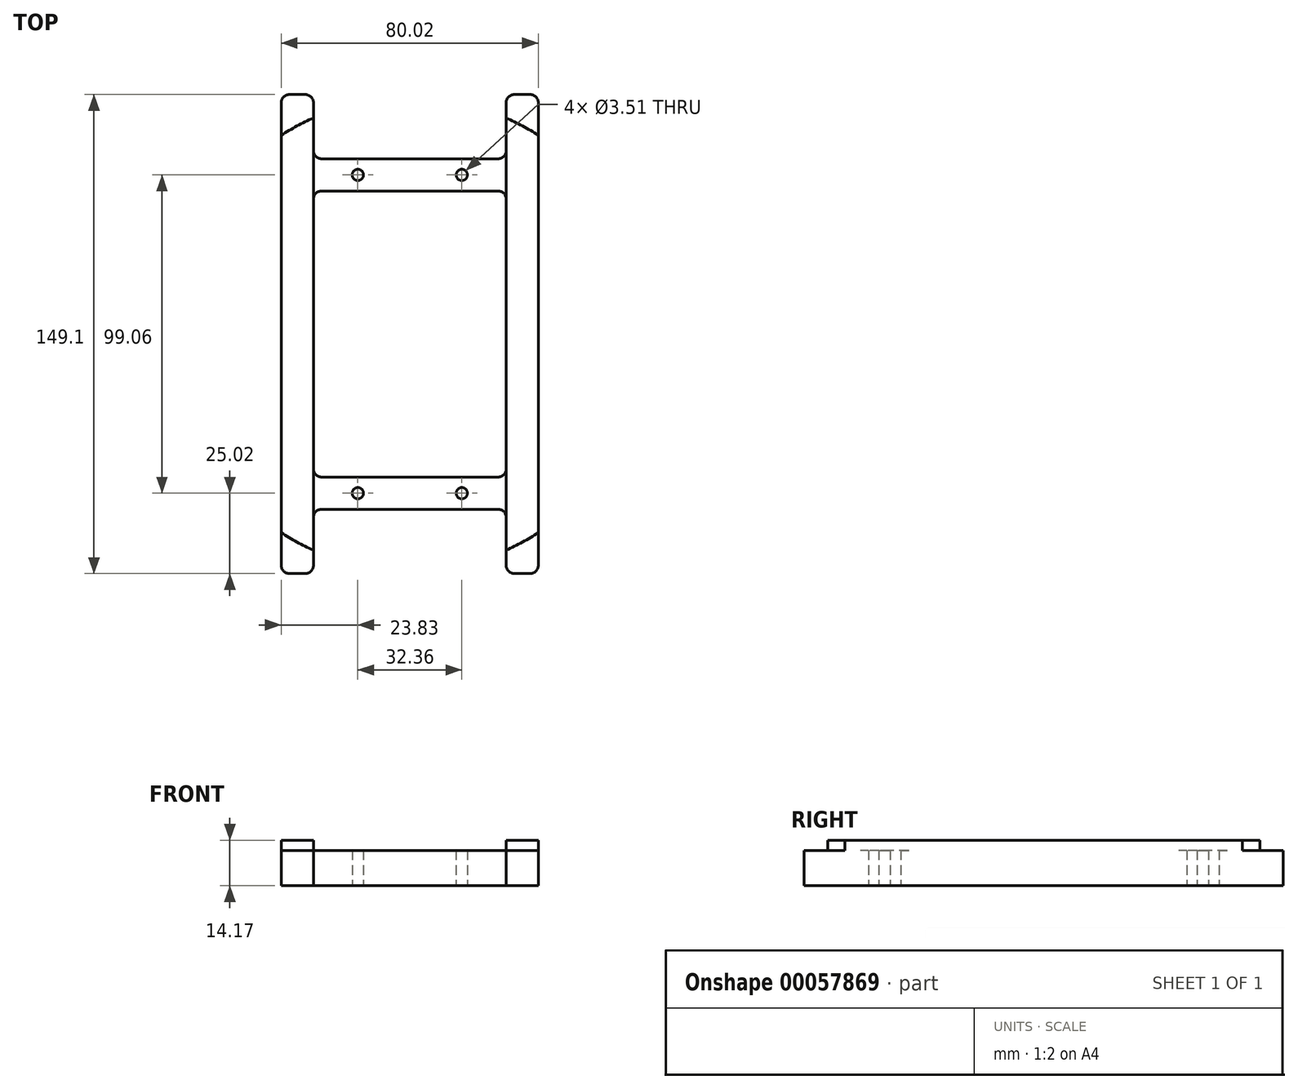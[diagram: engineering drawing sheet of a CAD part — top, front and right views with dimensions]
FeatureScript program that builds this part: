
annotation { "Feature Type Name" : "Feature", "Feature Type Description" : "" }
export const myFeature = defineFeature(function(context is Context, id is Id, definition is map)
    precondition{}
    {
        {
            var Q0;
            Q0=qCreatedBy(makeId("Top.planeOp"),FACE);
            var sketch = newSketch(context, id + "F0", { "sketchPlane" : qUnion([Q0])});
            skLineSegment(sketch, "E0.rect.bottom", {"start": v(30, 44.53) * mm, "end": v(-30, 44.53) * mm});
            skLineSegment(sketch, "E0.rect.top", {"start": v(30, -44.53) * mm, "end": v(-30, -44.53) * mm});
            skLineSegment(sketch, "E0.rect.left", {"start": v(30, 44.53) * mm, "end": v(30, -44.53) * mm});
            skLineSegment(sketch, "E0.rect.right", {"start": v(-30, 44.53) * mm, "end": v(-30, -44.53) * mm});
            skPoint(sketch, "E0.rect.middle", {"position": v(0, 0) * mm});
            skLineSegment(sketch, "E1.bottom", {"start": v(-30, 54.53) * mm, "end": v(30, 54.53) * mm});
            skLineSegment(sketch, "E1.top", {"start": v(-30, -54.53) * mm, "end": v(30, -54.53) * mm});
            skLineSegment(sketch, "E1.left", {"start": v(-40, 54.53) * mm, "end": v(-40, -54.53) * mm});
            skLineSegment(sketch, "E1.right", {"start": v(40, 54.53) * mm, "end": v(40, -54.53) * mm});
            skLineSegment(sketch, "E2.top", {"start": v(-40, 74.55) * mm, "end": v(-30, 74.55) * mm});
            skLineSegment(sketch, "E2.left", {"start": v(-40, 54.53) * mm, "end": v(-40, 74.55) * mm});
            skLineSegment(sketch, "E2.right", {"start": v(-30, 54.53) * mm, "end": v(-30, 74.55) * mm});
            skLineSegment(sketch, "E3.top", {"start": v(40, 74.55) * mm, "end": v(30, 74.55) * mm});
            skLineSegment(sketch, "E3.left", {"start": v(40, 54.53) * mm, "end": v(40, 74.55) * mm});
            skLineSegment(sketch, "E3.right", {"start": v(30, 54.53) * mm, "end": v(30, 74.55) * mm});
            skLineSegment(sketch, "E4.top", {"start": v(40, -74.55) * mm, "end": v(30, -74.55) * mm});
            skLineSegment(sketch, "E4.left", {"start": v(40, -54.53) * mm, "end": v(40, -74.55) * mm});
            skLineSegment(sketch, "E4.right", {"start": v(30, -54.53) * mm, "end": v(30, -74.55) * mm});
            skLineSegment(sketch, "E5.top", {"start": v(-40, -74.55) * mm, "end": v(-30, -74.55) * mm});
            skLineSegment(sketch, "E5.left", {"start": v(-40, -54.53) * mm, "end": v(-40, -74.55) * mm});
            skLineSegment(sketch, "E5.right", {"start": v(-30, -54.53) * mm, "end": v(-30, -74.55) * mm});
            skCircle(sketch, "E6", {"center": v(-16.18, 49.53) * mm, "radius": 1.75 * mm});
            skCircle(sketch, "E7", {"center": v(16.18, 49.53) * mm, "radius": 1.75 * mm});
            skCircle(sketch, "E8", {"center": v(-16.18, -49.53) * mm, "radius": 1.75 * mm});
            skCircle(sketch, "E9", {"center": v(16.18, -49.53) * mm, "radius": 1.75 * mm});
            skSolve(sketch);
        }
        {
            var Q0;
            Q0=makeQuery(id+"F0.imprint","IMPRINT",FACE,{"disambiguationData":[TD([[makeQuery(id+"F0.imprint","IMPRINT",EDGE,{"derivedFrom":sQuery(id+"F0.wireOp",EDGE,"E0.rect.bottom")}),-1.0]])]});
            extrude(context, id + "F1", {"entities" : qUnion([Q0]), "depth" : 11 * mm});
        }
        {
            var Q0;
            Q0=makeQuery(id+"F1.opExtrude","CAP_FACE",FACE,{"disambiguationData":[OSD([sQuery(id+"F0.wireOp",EDGE,"E0.rect.bottom"),sQuery(id+"F0.wireOp",EDGE,"E0.rect.top"),sQuery(id+"F0.wireOp",EDGE,"E0.rect.left"),sQuery(id+"F0.wireOp",EDGE,"E0.rect.right"),sQuery(id+"F0.wireOp",EDGE,"E1.bottom"),sQuery(id+"F0.wireOp",EDGE,"E1.top"),sQuery(id+"F0.wireOp",EDGE,"E1.left"),sQuery(id+"F0.wireOp",EDGE,"E1.right"),sQuery(id+"F0.wireOp",EDGE,"E2.top"),sQuery(id+"F0.wireOp",EDGE,"E2.left"),sQuery(id+"F0.wireOp",EDGE,"E2.right"),sQuery(id+"F0.wireOp",EDGE,"E3.top"),sQuery(id+"F0.wireOp",EDGE,"E3.left"),sQuery(id+"F0.wireOp",EDGE,"E3.right"),sQuery(id+"F0.wireOp",EDGE,"E4.top"),sQuery(id+"F0.wireOp",EDGE,"E4.left"),sQuery(id+"F0.wireOp",EDGE,"E4.right"),sQuery(id+"F0.wireOp",EDGE,"E5.top"),sQuery(id+"F0.wireOp",EDGE,"E5.left"),sQuery(id+"F0.wireOp",EDGE,"E5.right"),sQuery(id+"F0.wireOp",EDGE,"E6"),sQuery(id+"F0.wireOp",EDGE,"E7"),sQuery(id+"F0.wireOp",EDGE,"E8"),sQuery(id+"F0.wireOp",EDGE,"E9")])],"isStart":false});
            var sketch = newSketch(context, id + "F2", { "sketchPlane" : qUnion([Q0])});
            skLineSegment(sketch, "E10", {"start": v(-40, 61.85) * mm, "end": v(-40, -61.85) * mm});
            skLineSegment(sketch, "E11", {"start": v(-30, -67.28) * mm, "end": v(-30, 67.28) * mm});
            skPoint(sketch, "E12", {"position": v(-40, 0) * mm});
            skLineSegment(sketch, "E13", {"start": v(30, 67.28) * mm, "end": v(30, -67.28) * mm});
            skLineSegment(sketch, "E14", {"start": v(40, -61.85) * mm, "end": v(40, 61.85) * mm});
            skPoint(sketch, "E15", {"position": v(40, 0) * mm});
            skArc(sketch, "E16", {"start": v(-40, -61.85) * mm, "mid": v(-35.1, -64.76) * mm, "end": v(-30, -67.28) * mm});
            skArc(sketch, "E17.trimOffspring", {"start": v(40, 61.85) * mm, "mid": v(35.1, 64.76) * mm, "end": v(30, 67.28) * mm});
            skArc(sketch, "E18.trimOffspring", {"start": v(-30, 67.28) * mm, "mid": v(-35.1, 64.76) * mm, "end": v(-40, 61.85) * mm});
            skArc(sketch, "E19.trimOffspring", {"start": v(30, -67.28) * mm, "mid": v(35.1, -64.76) * mm, "end": v(40, -61.85) * mm});
            skSolve(sketch);
        }
        {
            var Q0;
            Q0=makeQuery(id+"F2.imprint","IMPRINT",FACE,{"disambiguationData":[TD([[makeQuery(id+"F2.imprint","IMPRINT",EDGE,{"derivedFrom":sQuery(id+"F2.wireOp",EDGE,"E10")}),-1.0]])]});
            var Q1;
            Q1=makeQuery(id+"F2.imprint","IMPRINT",FACE,{"disambiguationData":[TD([[makeQuery(id+"F2.imprint","IMPRINT",EDGE,{"derivedFrom":sQuery(id+"F2.wireOp",EDGE,"E14")}),-1.0]])]});
            extrude(context, id + "F3", {"entities" : qUnion([Q0, Q1]), "operationType" : NewBodyOperationType.ADD, "depth" : 3.17 * mm});
        }
        {
            var Q0;
            Q0=makeQuery(id+"F1.opExtrude","SWEPT_EDGE",EDGE,{"disambiguationData":[OSD([sQuery(id+"F0.wireOp",EDGE,"E0.rect.bottom"),sQuery(id+"F0.wireOp",EDGE,"E0.rect.left")])]});
            var Q1;
            Q1=makeQuery(id+"F1.opExtrude","SWEPT_EDGE",EDGE,{"disambiguationData":[OSD([sQuery(id+"F0.wireOp",EDGE,"E0.rect.bottom"),sQuery(id+"F0.wireOp",EDGE,"E0.rect.right")])]});
            var Q2;
            Q2=makeQuery(id+"F1.opExtrude","SWEPT_EDGE",EDGE,{"disambiguationData":[OSD([sQuery(id+"F0.wireOp",EDGE,"E1.bottom"),sQuery(id+"F0.wireOp",EDGE,"E3.right")])]});
            var Q3;
            Q3=makeQuery(id+"F1.opExtrude","SWEPT_EDGE",EDGE,{"disambiguationData":[OSD([sQuery(id+"F0.wireOp",EDGE,"E1.bottom"),sQuery(id+"F0.wireOp",EDGE,"E2.right")])]});
            var Q4;
            Q4=makeQuery(id+"F1.opExtrude","SWEPT_EDGE",EDGE,{"disambiguationData":[OSD([sQuery(id+"F0.wireOp",EDGE,"E2.top"),sQuery(id+"F0.wireOp",EDGE,"E2.right")])]});
            var Q5;
            Q5=makeQuery(id+"F1.opExtrude","SWEPT_EDGE",EDGE,{"disambiguationData":[OSD([sQuery(id+"F0.wireOp",EDGE,"E2.top"),sQuery(id+"F0.wireOp",EDGE,"E2.left")])]});
            var Q6;
            Q6=makeQuery(id+"F1.opExtrude","SWEPT_EDGE",EDGE,{"disambiguationData":[OSD([sQuery(id+"F0.wireOp",EDGE,"E3.top"),sQuery(id+"F0.wireOp",EDGE,"E3.right")])]});
            var Q7;
            Q7=makeQuery(id+"F1.opExtrude","SWEPT_EDGE",EDGE,{"disambiguationData":[OSD([sQuery(id+"F0.wireOp",EDGE,"E3.top"),sQuery(id+"F0.wireOp",EDGE,"E3.left")])]});
            var Q8;
            Q8=makeQuery(id+"F1.opExtrude","SWEPT_EDGE",EDGE,{"disambiguationData":[OSD([sQuery(id+"F0.wireOp",EDGE,"E4.top"),sQuery(id+"F0.wireOp",EDGE,"E4.right")])]});
            var Q9;
            Q9=makeQuery(id+"F1.opExtrude","SWEPT_EDGE",EDGE,{"disambiguationData":[OSD([sQuery(id+"F0.wireOp",EDGE,"E4.top"),sQuery(id+"F0.wireOp",EDGE,"E4.left")])]});
            var Q10;
            Q10=makeQuery(id+"F1.opExtrude","SWEPT_EDGE",EDGE,{"disambiguationData":[OSD([sQuery(id+"F0.wireOp",EDGE,"E5.top"),sQuery(id+"F0.wireOp",EDGE,"E5.right")])]});
            var Q11;
            Q11=makeQuery(id+"F1.opExtrude","SWEPT_EDGE",EDGE,{"disambiguationData":[OSD([sQuery(id+"F0.wireOp",EDGE,"E5.top"),sQuery(id+"F0.wireOp",EDGE,"E5.left")])]});
            var Q12;
            Q12=makeQuery(id+"F1.opExtrude","SWEPT_EDGE",EDGE,{"disambiguationData":[OSD([sQuery(id+"F0.wireOp",EDGE,"E1.top"),sQuery(id+"F0.wireOp",EDGE,"E5.right")])]});
            var Q13;
            Q13=makeQuery(id+"F1.opExtrude","SWEPT_EDGE",EDGE,{"disambiguationData":[OSD([sQuery(id+"F0.wireOp",EDGE,"E1.top"),sQuery(id+"F0.wireOp",EDGE,"E4.right")])]});
            var Q14;
            Q14=makeQuery(id+"F1.opExtrude","SWEPT_EDGE",EDGE,{"disambiguationData":[OSD([sQuery(id+"F0.wireOp",EDGE,"E0.rect.top"),sQuery(id+"F0.wireOp",EDGE,"E0.rect.left")])]});
            var Q15;
            Q15=makeQuery(id+"F1.opExtrude","SWEPT_EDGE",EDGE,{"disambiguationData":[OSD([sQuery(id+"F0.wireOp",EDGE,"E0.rect.top"),sQuery(id+"F0.wireOp",EDGE,"E0.rect.right")])]});
            fillet(context, id + "F4", {"entities" : qUnion([Q0, Q1, Q2, Q3, Q4, Q5, Q6, Q7, Q8, Q9, Q10, Q11, Q12, Q13, Q14, Q15]), "radius" : 2.54 * mm, "tangentPropagation" : true, "allowEdgeOverflow" : false});
        }
    });
